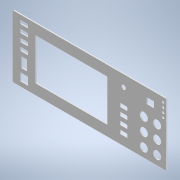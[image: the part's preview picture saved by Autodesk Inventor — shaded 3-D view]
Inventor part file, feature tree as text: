
AUTODESK INVENTOR PART (.ipt)
format: ipt  version: 2020.3 (Build 243373000, 373)  size: 308,224 bytes
history: native  units: mm
features: fillet x3, extrude x1, sketch x1
ambient origin geometry x8: Origin, YZ Plane, XZ Plane, XY Plane, X Axis, Y Axis, Z Axis, Center Point
bodies: Body1 (feature_tree)
feature tree (5):
  extrude  "Extrusion2"  Depth=84.0mm
  fillet  "Fillet1"  Radius=56.4mm
  fillet  "Fillet2"  Radius=97.22mm
  fillet  "Fillet3"  Radius=10.6mm
  sketch  "Sketch1"  dims[d0=207.0mm d1=84.0mm d4=56.4mm d5=97.22mm d6=10.6mm d7=10.0mm d8=6.0mm d9=18.0mm d10=18.0mm d11=11.0mm d12=18.0mm d13=95.04mm d14=53.86mm d15=5.19mm d16=3.98mm d17=67.07mm d18=105.42mm d21=10.0mm d22=12.0mm d23=12.0mm d24=13.9mm d25=7.5mm d26=5.5mm d27=5.0mm d28=5.5mm d29=5.5mm d30=5.5mm d31=5.5mm d32=10.0mm d33=6.0mm d34=22.0mm d35=10.0mm d36=8.0mm d37=3.2mm d38=3.2mm d39=3.2mm d40=3.2mm d41=6.0mm d42=6.0mm d43=6.0mm d44=4.0mm d45=5.0mm d46=5.5mm d47=5.5mm d48=5.5mm d49=10.0mm d50=5.5mm d51=5.5mm d52=6.0mm d53=1.6mm d54=0.0mm d55=1.0mm d56=0.75mm d57=0.5mm]
